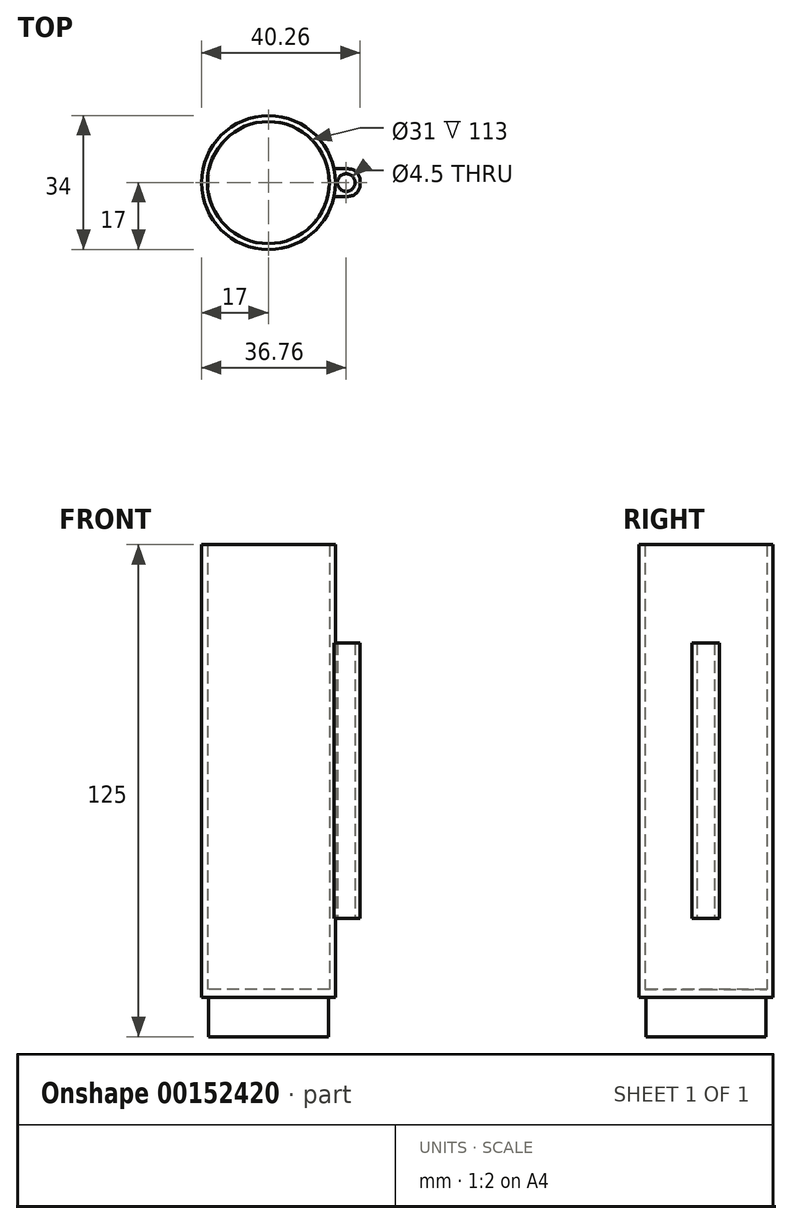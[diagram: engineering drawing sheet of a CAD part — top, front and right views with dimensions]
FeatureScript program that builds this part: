
annotation { "Feature Type Name" : "Feature", "Feature Type Description" : "" }
export const myFeature = defineFeature(function(context is Context, id is Id, definition is map)
    precondition{}
    {
        {
            var Q0;
            Q0=qCreatedBy(makeId("Top.planeOp"),FACE);
            cPlane(context, id + "F0", {"entities" : qUnion([Q0]), "cplaneType" : CPlaneType.OFFSET, "offset" : (107) * mm, "width" : 150 * mm, "height" : 150 * mm});
        }
        {
            var Q0;
            Q0=qCreatedBy(id+"F0.planeOp",FACE);
            var sketch = newSketch(context, id + "F1", { "sketchPlane" : qUnion([Q0])});
            skCircle(sketch, "E0", {"center": v(0, 0) * mm, "radius": 17 * mm});
            skCircle(sketch, "E1", {"center": v(0, 0) * mm, "radius": 15.5 * mm});
            skSolve(sketch);
        }
        {
            var Q0;
            Q0=qSketchRegion(id+"F1",true);
            extrude(context, id + "F2", {"entities" : qUnion([Q0]), "depth" : 115 * mm});
        }
        {
            var Q0;
            Q0=qCreatedBy(id+"F0.planeOp",FACE);
            var sketch = newSketch(context, id + "F3", { "sketchPlane" : qUnion([Q0])});
            skCircle(sketch, "E2.0", {"center": v(0, 0) * mm, "radius": 17 * mm});
            skSolve(sketch);
        }
        {
            var Q0;
            Q0=makeQuery(id+"F3.imprint","IMPRINT",FACE,{"disambiguationData":[TD([[makeQuery(id+"F3.imprint","IMPRINT",EDGE,{"derivedFrom":sQuery(id+"F3.wireOp",EDGE,"E2.0")}),1.0]])]});
            extrude(context, id + "F4", {"entities" : qUnion([Q0]), "operationType" : NewBodyOperationType.ADD, "depth" : 2 * mm});
        }
        {
            var Q0;
            Q0=makeQuery(id+"F4.boolean.opBoolean","MERGE",FACE,{"derivedFrom":[makeQuery(id+"F2.opExtrude","CAP_FACE",FACE,{"disambiguationData":[OSD([sQuery(id+"F1.wireOp",EDGE,"E0"),sQuery(id+"F1.wireOp",EDGE,"E1")])],"isStart":true}),makeQuery(id+"F4.opExtrude","CAP_FACE",FACE,{"disambiguationData":[OSD([sQuery(id+"F3.wireOp",EDGE,"E2.0")])],"isStart":true})]});
            var sketch = newSketch(context, id + "F5", { "sketchPlane" : qUnion([Q0])});
            skCircle(sketch, "E3", {"center": v(0, 0) * mm, "radius": 15.25 * mm});
            skSolve(sketch);
        }
        {
            var Q0;
            Q0=qSketchRegion(id+"F5",true);
            extrude(context, id + "F6", {"entities" : qUnion([Q0]), "operationType" : NewBodyOperationType.ADD, "depth" : 10 * mm});
        }
        {
            var Q0;
            Q0=qCreatedBy(id+"F0.planeOp",FACE);
            cPlane(context, id + "F7", {"entities" : qUnion([Q0]), "cplaneType" : CPlaneType.OFFSET, "offset" : 20 * mm, "width" : 150 * mm, "height" : 150 * mm});
        }
        {
            var Q0;
            Q0=qCreatedBy(id+"F7.planeOp",FACE);
            var sketch = newSketch(context, id + "F8", { "sketchPlane" : qUnion([Q0])});
            skLineSegment(sketch, "E4.bottom", {"start": v(16.26, 3.5) * mm, "end": v(20.26, 3.5) * mm});
            skLineSegment(sketch, "E4.top", {"start": v(16.26, -3.5) * mm, "end": v(20.26, -3.5) * mm});
            skLineSegment(sketch, "E4.left", {"start": v(16.26, 3.5) * mm, "end": v(16.26, -3.5) * mm});
            skLineSegment(sketch, "E4.right", {"start": v(23.26, 0.5) * mm, "end": v(23.26, -0.5) * mm});
            skPoint(sketch, "E5", {"position": v(16.26, 0) * mm});
            skCircle(sketch, "E6", {"center": v(19.76, 0) * mm, "radius": 2.25 * mm});
            skPoint(sketch, "E7.visualSharp", {"position": v(23.26, 3.5) * mm});
            skArc(sketch, "E7.filletArc", {"start": v(23.26, 0.5) * mm, "mid": v(22.38, 2.62) * mm, "end": v(20.26, 3.5) * mm});
            skPoint(sketch, "E8.visualSharp", {"position": v(23.26, -3.5) * mm});
            skArc(sketch, "E8.filletArc", {"start": v(20.26, -3.5) * mm, "mid": v(22.38, -2.62) * mm, "end": v(23.26, -0.5) * mm});
            skSolve(sketch);
        }
        {
            var Q0;
            Q0=qSketchRegion(id+"F8",true);
            extrude(context, id + "F9", {"entities" : qUnion([Q0]), "depth" : 70 * mm});
        }
        {
            var Q0;
            Q0=makeQuery(id+"F2.opExtrude","SWEPT_BODY",BODY,{"disambiguationData":[OSD([sQuery(id+"F1.wireOp",EDGE,"E0"),sQuery(id+"F1.wireOp",EDGE,"E1")])]});
            var Q1;
            Q1=makeQuery(id+"F9.opExtrude","SWEPT_BODY",BODY,{"disambiguationData":[OSD([sQuery(id+"F8.wireOp",EDGE,"E4.bottom"),sQuery(id+"F8.wireOp",EDGE,"E4.top"),sQuery(id+"F8.wireOp",EDGE,"E4.left"),sQuery(id+"F8.wireOp",EDGE,"E4.right"),sQuery(id+"F8.wireOp",EDGE,"E6"),sQuery(id+"F8.wireOp",EDGE,"E7.filletArc"),sQuery(id+"F8.wireOp",EDGE,"E8.filletArc")])]});
            booleanBodies(context, id + "F10", {"operationType" : BooleanOperationType.SUBTRACTION, "tools" : qUnion([Q0]), "targets" : qUnion([Q1]), "keepTools" : true});
        }
    });
